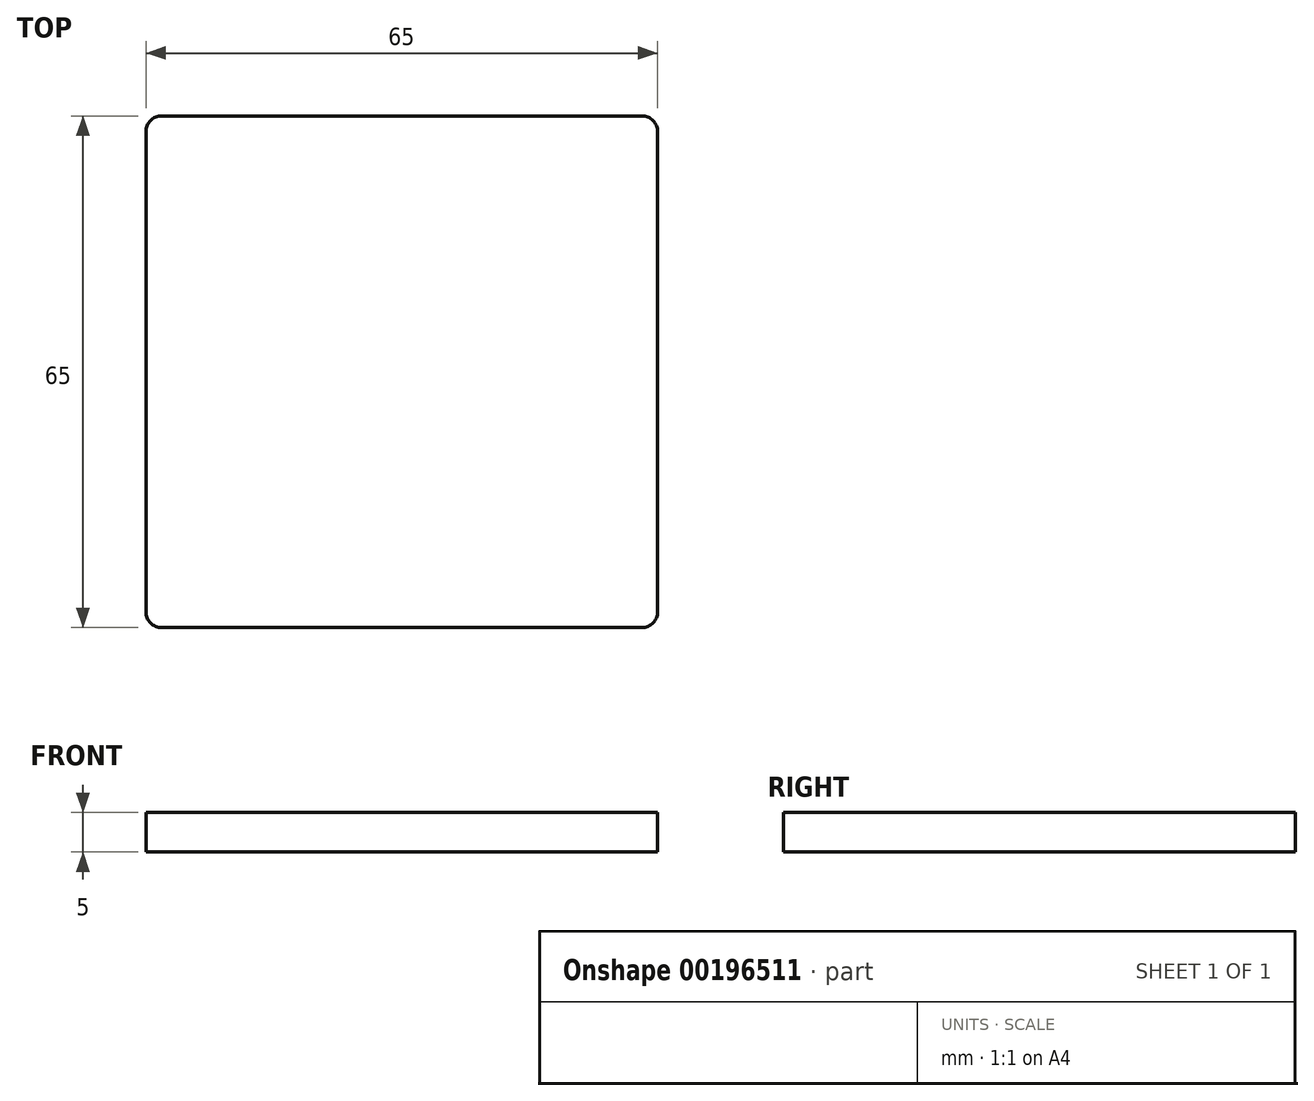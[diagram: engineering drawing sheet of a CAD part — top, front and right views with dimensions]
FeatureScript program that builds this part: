
annotation { "Feature Type Name" : "Feature", "Feature Type Description" : "" }
export const myFeature = defineFeature(function(context is Context, id is Id, definition is map)
    precondition{}
    {
        {
            var Q0;
            Q0=qCreatedBy(makeId("Top.planeOp"),FACE);
            var sketch = newSketch(context, id + "F0", { "sketchPlane" : qUnion([Q0])});
            skLineSegment(sketch, "E0.bottom", {"start": v(30.5, -32.5) * mm, "end": v(-30.5, -32.5) * mm});
            skLineSegment(sketch, "E0.top", {"start": v(30.5, 32.5) * mm, "end": v(-30.5, 32.5) * mm});
            skLineSegment(sketch, "E0.left", {"start": v(32.5, -30.5) * mm, "end": v(32.5, 30.5) * mm});
            skLineSegment(sketch, "E0.right", {"start": v(-32.5, -30.5) * mm, "end": v(-32.5, 30.5) * mm});
            skPoint(sketch, "E0.middle", {"position": v(0, 0) * mm});
            skPoint(sketch, "E1.visualSharp", {"position": v(-32.5, 32.5) * mm});
            skArc(sketch, "E1.filletArc", {"start": v(-30.5, 32.5) * mm, "mid": v(-31.91, 31.91) * mm, "end": v(-32.5, 30.5) * mm});
            skPoint(sketch, "E2.visualSharp", {"position": v(32.5, 32.5) * mm});
            skArc(sketch, "E2.filletArc", {"start": v(32.5, 30.5) * mm, "mid": v(31.91, 31.91) * mm, "end": v(30.5, 32.5) * mm});
            skPoint(sketch, "E3.visualSharp", {"position": v(-32.5, -32.5) * mm});
            skArc(sketch, "E3.filletArc", {"start": v(-32.5, -30.5) * mm, "mid": v(-31.91, -31.91) * mm, "end": v(-30.5, -32.5) * mm});
            skPoint(sketch, "E4.visualSharp", {"position": v(32.5, -32.5) * mm});
            skArc(sketch, "E4.filletArc", {"start": v(30.5, -32.5) * mm, "mid": v(31.91, -31.91) * mm, "end": v(32.5, -30.5) * mm});
            skSolve(sketch);
        }
        {
            var Q0;
            Q0=makeQuery(id+"F0.imprint","IMPRINT",FACE,{"disambiguationData":[TD([[makeQuery(id+"F0.imprint","IMPRINT",EDGE,{"derivedFrom":sQuery(id+"F0.wireOp",EDGE,"E0.bottom")}),-1.0]])]});
            extrude(context, id + "F1", {"entities" : qUnion([Q0]), "depth" : 5 * mm});
        }
    });
